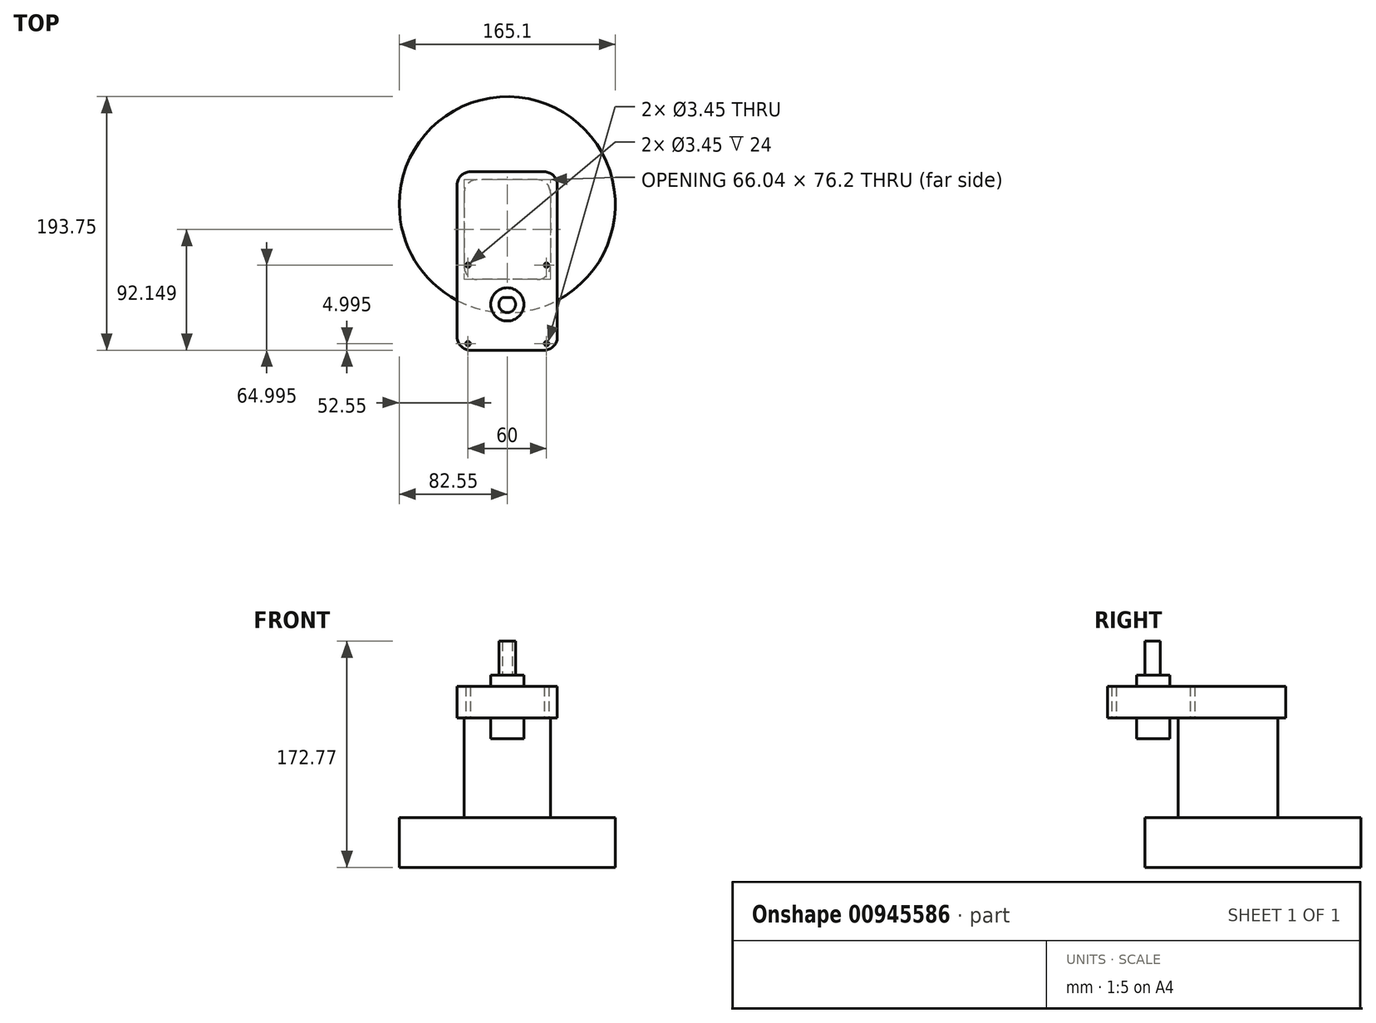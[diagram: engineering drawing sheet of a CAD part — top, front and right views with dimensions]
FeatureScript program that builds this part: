
annotation { "Feature Type Name" : "Feature", "Feature Type Description" : "" }
export const myFeature = defineFeature(function(context is Context, id is Id, definition is map)
    precondition{}
    {
        {
            var Q0;
            Q0=qCreatedBy(makeId("Top.planeOp"),FACE);
            var sketch = newSketch(context, id + "F0", { "sketchPlane" : qUnion([Q0])});
            skCircle(sketch, "E0", {"center": v(0, -33.17) * mm, "radius": 6.35 * mm, "construction": true});
            skCircle(sketch, "E1", {"center": v(30, -3.17) * mm, "radius": 1.73 * mm});
            skCircle(sketch, "E2", {"center": v(30, -63.17) * mm, "radius": 1.73 * mm});
            skCircle(sketch, "E3", {"center": v(-30, -63.17) * mm, "radius": 1.73 * mm});
            skCircle(sketch, "E4", {"center": v(-30, -3.17) * mm, "radius": 1.73 * mm});
            skLineSegment(sketch, "E5", {"start": v(30, -3.17) * mm, "end": v(-30, -63.17) * mm, "construction": true});
            skLineSegment(sketch, "E6", {"start": v(-30, -3.17) * mm, "end": v(30, -63.17) * mm, "construction": true});
            skLineSegment(sketch, "E7.bottom", {"start": v(-38.28, -68.17) * mm, "end": v(38.29, -68.17) * mm});
            skLineSegment(sketch, "E7.top", {"start": v(-38.29, 68.18) * mm, "end": v(38.28, 68.18) * mm});
            skLineSegment(sketch, "E7.left", {"start": v(-38.28, -68.17) * mm, "end": v(-38.29, 68.18) * mm});
            skLineSegment(sketch, "E7.right", {"start": v(38.29, -68.17) * mm, "end": v(38.28, 68.18) * mm});
            skPoint(sketch, "E7.middle", {"position": v(0, 0) * mm});
            skSolve(sketch);
        }
        {
            var Q0;
            Q0=qSketchRegion(id+"F0",true);
            extrude(context, id + "F1", {"entities" : qUnion([Q0]), "depth" : 24 * mm, "offsetDistance" : 25 * mm});
        }
        {
            var Q0;
            Q0=makeQuery(id+"F1.opExtrude","CAP_FACE",FACE,{"disambiguationData":[OSD([sQuery(id+"F0.wireOp",EDGE,"E1"),sQuery(id+"F0.wireOp",EDGE,"E2"),sQuery(id+"F0.wireOp",EDGE,"E3"),sQuery(id+"F0.wireOp",EDGE,"E4"),sQuery(id+"F0.wireOp",EDGE,"E7.bottom"),sQuery(id+"F0.wireOp",EDGE,"E7.top"),sQuery(id+"F0.wireOp",EDGE,"E7.left"),sQuery(id+"F0.wireOp",EDGE,"E7.right")])],"isStart":false});
            var sketch = newSketch(context, id + "F2", { "sketchPlane" : qUnion([Q0])});
            skCircle(sketch, "E8", {"center": v(0, -33.17) * mm, "radius": 12.7 * mm});
            skSolve(sketch);
        }
        {
            var Q0;
            Q0=qSketchRegion(id+"F2",true);
            extrude(context, id + "F3", {"entities" : qUnion([Q0]), "operationType" : NewBodyOperationType.ADD, "depth" : 8.47 * mm, "offsetDistance" : 25 * mm, "hasSecondDirection" : true, "secondDirectionOppositeDirection" : true, "secondDirectionDepth" : 40 * mm});
        }
        {
            var Q0;
            Q0=makeQuery(id+"F3.opExtrude","CAP_FACE",FACE,{"disambiguationData":[OSD([sQuery(id+"F2.wireOp",EDGE,"E8")])],"isStart":false});
            var sketch = newSketch(context, id + "F4", { "sketchPlane" : qUnion([Q0])});
            skArc(sketch, "E9", {"start": v(3.71, -28.02) * mm, "mid": v(0, -39.52) * mm, "end": v(-3.71, -28.02) * mm});
            skLineSegment(sketch, "E10", {"start": v(-3.71, -28.02) * mm, "end": v(3.71, -28.02) * mm});
            skSolve(sketch);
        }
        {
            var Q0;
            Q0=qSketchRegion(id+"F4",true);
            extrude(context, id + "F5", {"entities" : qUnion([Q0]), "operationType" : NewBodyOperationType.ADD, "depth" : 26 * mm, "offsetDistance" : 25 * mm});
        }
        {
            var Q0;
            Q0=makeQuery(id+"F1.opExtrude","CAP_FACE",FACE,{"disambiguationData":[OSD([sQuery(id+"F0.wireOp",EDGE,"E1"),sQuery(id+"F0.wireOp",EDGE,"E2"),sQuery(id+"F0.wireOp",EDGE,"E3"),sQuery(id+"F0.wireOp",EDGE,"E4"),sQuery(id+"F0.wireOp",EDGE,"E7.bottom"),sQuery(id+"F0.wireOp",EDGE,"E7.top"),sQuery(id+"F0.wireOp",EDGE,"E7.left"),sQuery(id+"F0.wireOp",EDGE,"E7.right")])],"isStart":true});
            var sketch = newSketch(context, id + "F6", { "sketchPlane" : qUnion([Q0])});
            skLineSegment(sketch, "E11.bottom", {"start": v(33.02, -62.08) * mm, "end": v(-33.02, -62.08) * mm});
            skLineSegment(sketch, "E11.top", {"start": v(33.02, 14.12) * mm, "end": v(-33.02, 14.12) * mm});
            skLineSegment(sketch, "E11.left", {"start": v(33.02, -62.08) * mm, "end": v(33.02, 14.12) * mm});
            skLineSegment(sketch, "E11.right", {"start": v(-33.02, -62.08) * mm, "end": v(-33.02, 14.12) * mm});
            skPoint(sketch, "E11.middle", {"position": v(0, -23.98) * mm});
            skSolve(sketch);
        }
        {
            var Q0;
            Q0=qSketchRegion(id+"F6",true);
            extrude(context, id + "F7", {"entities" : qUnion([Q0]), "operationType" : NewBodyOperationType.ADD, "depth" : 76.2 * mm, "offsetDistance" : 25 * mm});
        }
        {
            var Q0;
            Q0=makeQuery(id+"F7.opExtrude","CAP_FACE",FACE,{"disambiguationData":[OSD([sQuery(id+"F6.wireOp",EDGE,"E11.bottom"),sQuery(id+"F6.wireOp",EDGE,"E11.top"),sQuery(id+"F6.wireOp",EDGE,"E11.left"),sQuery(id+"F6.wireOp",EDGE,"E11.right")])],"isStart":false});
            var sketch = newSketch(context, id + "F8", { "sketchPlane" : qUnion([Q0])});
            skCircle(sketch, "E12", {"center": v(0, -43.03) * mm, "radius": 82.55 * mm});
            skSolve(sketch);
        }
        {
            var Q0;
            Q0=qSketchRegion(id+"F8",true);
            extrude(context, id + "F9", {"entities" : qUnion([Q0]), "operationType" : NewBodyOperationType.ADD, "depth" : 38.1 * mm, "offsetDistance" : 25 * mm});
        }
        {
            var Q0;
            Q0=makeQuery(id+"F7.opExtrude","SWEPT_EDGE",EDGE,{"disambiguationData":[OSD([sQuery(id+"F6.wireOp",EDGE,"E11.bottom"),sQuery(id+"F6.wireOp",EDGE,"E11.right")])]});
            var Q1;
            Q1=makeQuery(id+"F7.opExtrude","SWEPT_EDGE",EDGE,{"disambiguationData":[OSD([sQuery(id+"F6.wireOp",EDGE,"E11.top"),sQuery(id+"F6.wireOp",EDGE,"E11.right")])]});
            var Q2;
            Q2=makeQuery(id+"F7.opExtrude","SWEPT_EDGE",EDGE,{"disambiguationData":[OSD([sQuery(id+"F6.wireOp",EDGE,"E11.bottom"),sQuery(id+"F6.wireOp",EDGE,"E11.left")])]});
            var Q3;
            Q3=makeQuery(id+"F7.opExtrude","SWEPT_EDGE",EDGE,{"disambiguationData":[OSD([sQuery(id+"F6.wireOp",EDGE,"E11.top"),sQuery(id+"F6.wireOp",EDGE,"E11.left")])]});
            var Q4;
            Q4=makeQuery(id+"F1.opExtrude","SWEPT_EDGE",EDGE,{"disambiguationData":[OSD([sQuery(id+"F0.wireOp",EDGE,"E7.top"),sQuery(id+"F0.wireOp",EDGE,"E7.right")])]});
            var Q5;
            Q5=makeQuery(id+"F1.opExtrude","SWEPT_EDGE",EDGE,{"disambiguationData":[OSD([sQuery(id+"F0.wireOp",EDGE,"E7.top"),sQuery(id+"F0.wireOp",EDGE,"E7.left")])]});
            var Q6;
            Q6=makeQuery(id+"F1.opExtrude","SWEPT_EDGE",EDGE,{"disambiguationData":[OSD([sQuery(id+"F0.wireOp",EDGE,"E7.bottom"),sQuery(id+"F0.wireOp",EDGE,"E7.left")])]});
            var Q7;
            Q7=makeQuery(id+"F1.opExtrude","SWEPT_EDGE",EDGE,{"disambiguationData":[OSD([sQuery(id+"F0.wireOp",EDGE,"E7.bottom"),sQuery(id+"F0.wireOp",EDGE,"E7.right")])]});
            fillet(context, id + "F10", {"entities" : qUnion([Q0, Q1, Q2, Q3, Q4, Q5, Q6, Q7]), "radius" : 10 * mm, "tangentPropagation" : true, "allowEdgeOverflow" : false});
        }
    });
